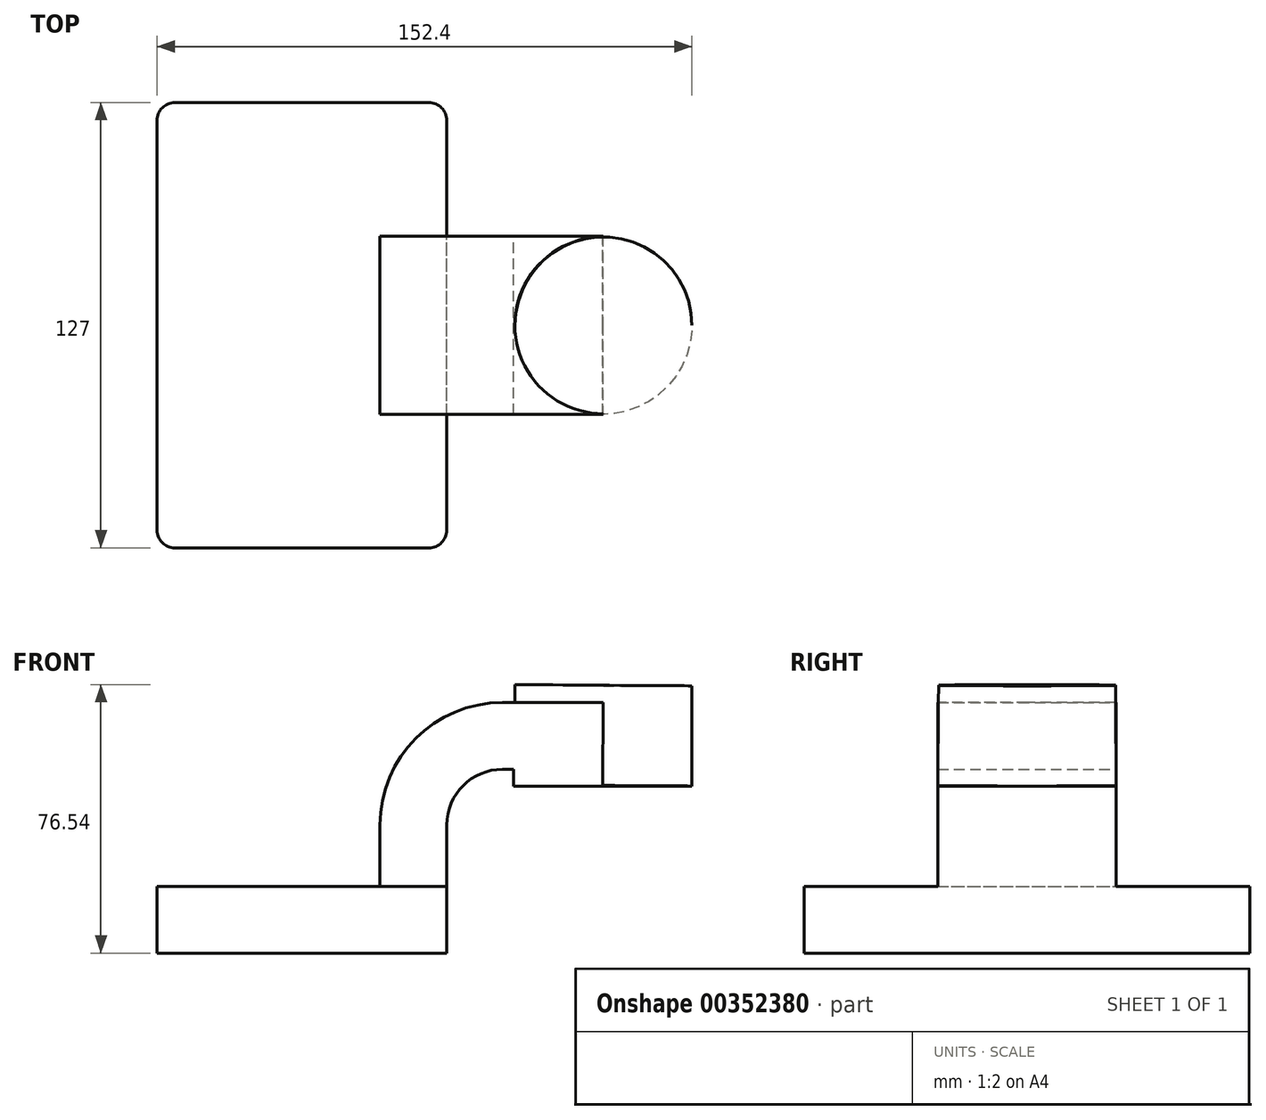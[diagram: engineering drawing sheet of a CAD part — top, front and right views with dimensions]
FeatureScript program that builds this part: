
annotation { "Feature Type Name" : "Feature", "Feature Type Description" : "" }
export const myFeature = defineFeature(function(context is Context, id is Id, definition is map)
    precondition{}
    {
        {
            var Q0;
            Q0=qCreatedBy(makeId("Front.planeOp"),FACE);
            var sketch = newSketch(context, id + "F0", { "sketchPlane" : qUnion([Q0])});
            skLineSegment(sketch, "E0.bottom", {"start": v(41.27, 9.53) * mm, "end": v(-41.28, 9.53) * mm});
            skLineSegment(sketch, "E0.top", {"start": v(41.28, -9.52) * mm, "end": v(-41.27, -9.52) * mm});
            skLineSegment(sketch, "E0.left", {"start": v(41.28, 9.53) * mm, "end": v(41.28, -9.52) * mm});
            skLineSegment(sketch, "E0.right", {"start": v(-41.28, 9.53) * mm, "end": v(-41.27, -9.52) * mm});
            skPoint(sketch, "E0.middle", {"position": v(0, 0) * mm});
            skLineSegment(sketch, "E1.bottom", {"start": v(111.13, 38.1) * mm, "end": v(60.33, 38.1) * mm});
            skLineSegment(sketch, "E1.top", {"start": v(111.13, 66.68) * mm, "end": v(60.33, 66.68) * mm});
            skLineSegment(sketch, "E1.left", {"start": v(111.13, 38.1) * mm, "end": v(111.13, 66.68) * mm});
            skLineSegment(sketch, "E1.right", {"start": v(60.33, 38.1) * mm, "end": v(60.33, 66.68) * mm});
            skPoint(sketch, "E1.middle", {"position": v(85.72, 52.39) * mm});
            skLineSegment(sketch, "E2", {"start": v(41.27, 9.53) * mm, "end": v(41.27, 27) * mm});
            skArc(sketch, "E3", {"start": v(41.27, 27) * mm, "mid": v(45.92, 38.23) * mm, "end": v(57.15, 42.88) * mm});
            skLineSegment(sketch, "E4", {"start": v(57.15, 42.88) * mm, "end": v(85.58, 42.88) * mm});
            skLineSegment(sketch, "E5.0", {"start": v(57.15, 61.93) * mm, "end": v(85.92, 61.93) * mm});
            skArc(sketch, "E5.1", {"start": v(22.22, 27) * mm, "mid": v(32.45, 51.7) * mm, "end": v(57.15, 61.93) * mm});
            skLineSegment(sketch, "E5.2", {"start": v(22.22, 9.53) * mm, "end": v(22.22, 27) * mm});
            skLineSegment(sketch, "E6", {"start": v(85.73, 38.1) * mm, "end": v(85.92, 66.68) * mm});
            skFitSpline(sketch, "E7", {"points": [v(-41.27, 9.53) * mm, v(57.15, 61.93) * mm], "startDerivative": vector(89.13, 117.13) * mm, "endDerivative": vector(110.67, -26.26) * mm});
            skSolve(sketch);
        }
        {
            var Q0;
            Q0=makeQuery(id+"F0.imprint","IMPRINT",FACE,{"disambiguationData":[TD([[makeQuery(id+"F0.imprint","IMPRINT",EDGE,{"derivedFrom":sQuery(id+"F0.wireOp",EDGE,"E0.top")}),-1.0]])]});
            extrude(context, id + "F1", {"entities" : qUnion([Q0]), "endBound" : BoundingType.SYMMETRIC, "depth" : 127 * mm});
        }
        {
            var Q0;
            {var subQ1=sQuery(id+"F0.wireOp",EDGE,"E2");Q0=makeQuery(id+"F0.imprint","IMPRINT",FACE,{"disambiguationData":[TD([[makeQuery(id+"F0.imprint","IMPRINT",EDGE,{"derivedFrom":subQ1}),1.0]])]});}
            var Q1;
            {var subQ1=sQuery(id+"F0.wireOp",EDGE,"E1.right");var subQ5=sQuery(id+"F0.wireOp",EDGE,"E1.bottom");var subQ6=makeQuery(id+"F0.imprint","INTERSECT",VERTEX,{"derivedFrom":[subQ5,subQ1]});Q1=makeQuery(id+"F0.imprint","IMPRINT",FACE,{"disambiguationData":[TD([[makeQuery(id+"F0.imprint","IMPRINT",EDGE,{"disambiguationData":[TD([[subQ6,1.0]])],"derivedFrom":subQ5}),-1.0]])]});}
            extrude(context, id + "F2", {"entities" : qUnion([Q0, Q1]), "operationType" : NewBodyOperationType.ADD, "endBound" : BoundingType.SYMMETRIC, "depth" : 50.8 * mm});
        }
        {
            var Q0;
            Q0=makeQuery(id+"F0.imprint","IMPRINT",FACE,{"disambiguationData":[TD([[makeQuery(id+"F0.imprint","IMPRINT",EDGE,{"derivedFrom":sQuery(id+"F0.wireOp",EDGE,"E5.1")}),1.0]])]});
            extrude(context, id + "F3", {"entities" : qUnion([Q0]), "operationType" : NewBodyOperationType.ADD, "endBound" : BoundingType.SYMMETRIC, "depth" : 15.88 * mm});
        }
        {
            var Q0;
            {var subQ0=sQuery(id+"F0.wireOp",EDGE,"E1.left");Q0=makeQuery(id+"F0.imprint","IMPRINT",FACE,{"disambiguationData":[TD([[makeQuery(id+"F0.imprint","IMPRINT",EDGE,{"derivedFrom":subQ0}),1.0]])]});}
            var Q1;
            Q1=sQuery(id+"F0.wireOp",EDGE,"E6");
            revolve(context, id + "F4", {"operationType" : NewBodyOperationType.ADD, "entities" : qUnion([Q0]), "axis" : qUnion([Q1]), "revolveType" : RevolveType.FULL});
        }
        {
            var Q0;
            Q0=makeQuery(id+"F1.opExtrude","CAP_EDGE",EDGE,{"disambiguationData":[OSD([sQuery(id+"F0.wireOp",EDGE,"E0.left")])],"isStart":false});
            var Q1;
            Q1=makeQuery(id+"F1.opExtrude","CAP_EDGE",EDGE,{"disambiguationData":[OSD([sQuery(id+"F0.wireOp",EDGE,"E0.right")])],"isStart":false});
            var Q2;
            Q2=makeQuery(id+"F1.opExtrude","CAP_EDGE",EDGE,{"disambiguationData":[OSD([sQuery(id+"F0.wireOp",EDGE,"E0.left")])],"isStart":true});
            var Q3;
            Q3=makeQuery(id+"F1.opExtrude","CAP_EDGE",EDGE,{"disambiguationData":[OSD([sQuery(id+"F0.wireOp",EDGE,"E0.right")])],"isStart":true});
            fillet(context, id + "F5", {"entities" : qUnion([Q0, Q1, Q2, Q3]), "radius" : 5.08 * mm, "tangentPropagation" : true, "allowEdgeOverflow" : false});
        }
    });
